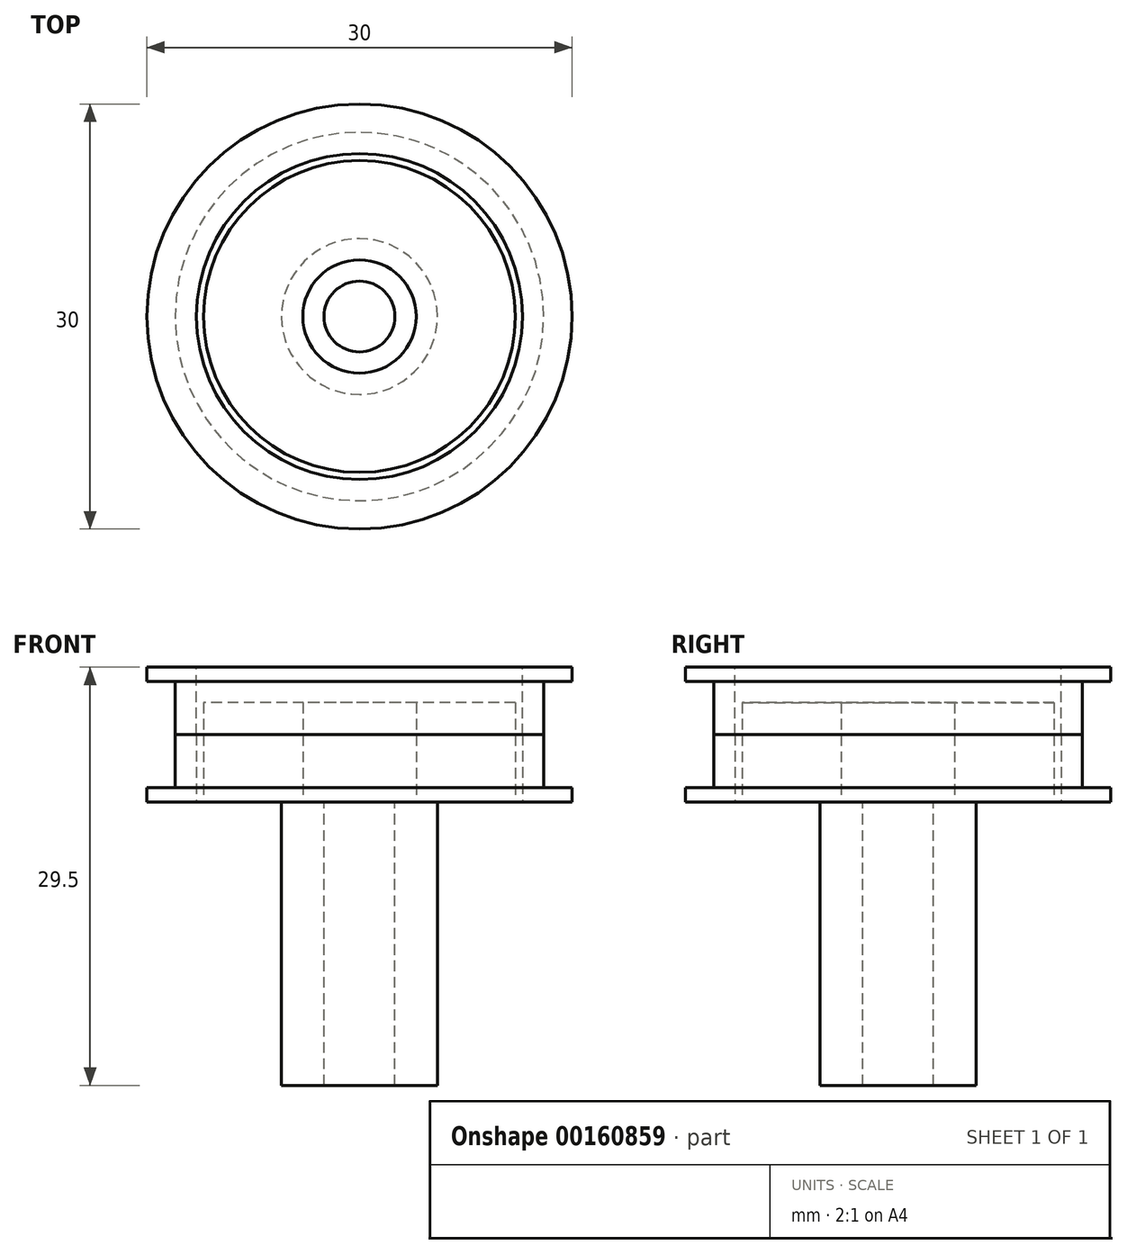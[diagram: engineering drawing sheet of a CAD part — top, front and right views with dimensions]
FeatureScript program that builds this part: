
annotation { "Feature Type Name" : "Feature", "Feature Type Description" : "" }
export const myFeature = defineFeature(function(context is Context, id is Id, definition is map)
    precondition{}
    {
        {
            var Q0;
            Q0=qCreatedBy(makeId("Top.planeOp"),FACE);
            var sketch = newSketch(context, id + "F0", { "sketchPlane" : qUnion([Q0])});
            skCircle(sketch, "E0", {"center": v(0, 0) * mm, "radius": 4 * mm});
            skCircle(sketch, "E1", {"center": v(0, 0) * mm, "radius": 11 * mm});
            skSolve(sketch);
        }
        {
            var Q0;
            Q0 = qSketchRegion(id + "F0", true);
            extrude(context, id + "F1", {"entities" : qUnion([Q0]), "depth" : 7 * mm});
        }
        {
            var Q0;
            Q0=qCreatedBy(makeId("Top.planeOp"),FACE);
            var Q1;
            Q1=qCreatedBy(makeId("Top.planeOp"),FACE);
            var sketch = newSketch(context, id + "F2", { "sketchPlane" : qUnion([Q0, Q1])});
            skCircle(sketch, "E2", {"center": v(0, 0) * mm, "radius": 2.5 * mm});
            skCircle(sketch, "E3", {"center": v(0, 0) * mm, "radius": 5.5 * mm});
            skSolve(sketch);
        }
        {
            var Q0;
            Q0 = qSketchRegion(id + "F2", true);
            extrude(context, id + "F3", {"entities" : qUnion([Q0]), "oppositeDirection" : true, "depth" : 20 * mm});
        }
        {
            var Q0;
            Q0=qCreatedBy(makeId("Top.planeOp"),FACE);
            var sketch = newSketch(context, id + "F4", { "sketchPlane" : qUnion([Q0])});
            skCircle(sketch, "E4", {"center": v(0, 0) * mm, "radius": 11.5 * mm});
            skCircle(sketch, "E5", {"center": v(0, 0) * mm, "radius": 13 * mm});
            skSolve(sketch);
        }
        {
            var Q0;
            Q0 = qSketchRegion(id + "F4", true);
            extrude(context, id + "F5", {"entities" : qUnion([Q0]), "depth" : 4.75 * mm});
        }
        {
            var Q0;
            Q0=qCreatedBy(makeId("Top.planeOp"),FACE);
            var sketch = newSketch(context, id + "F6", { "sketchPlane" : qUnion([Q0])});
            skCircle(sketch, "E6", {"center": v(0, 0) * mm, "radius": 13 * mm});
            skCircle(sketch, "E7", {"center": v(0, 0) * mm, "radius": 15 * mm});
            skSolve(sketch);
        }
        {
            var Q0;
            Q0 = qSketchRegion(id + "F6", true);
            extrude(context, id + "F7", {"entities" : qUnion([Q0]), "operationType" : NewBodyOperationType.ADD, "depth" : 1 * mm});
        }
        {
            var Q0;
            Q0=makeQuery(id+"F5.opExtrude","SWEPT_BODY",BODY,{"disambiguationData":[OSD([sQuery(id+"F4.wireOp",EDGE,"E4"),sQuery(id+"F4.wireOp",EDGE,"E5")])]});
            var Q1;
            Q1=makeQuery(id+"F5.opExtrude","CAP_FACE",FACE,{"disambiguationData":[OSD([sQuery(id+"F4.wireOp",EDGE,"E4"),sQuery(id+"F4.wireOp",EDGE,"E5")])],"isStart":false});
            mirror(context, id + "F8", {"operationType" : NewBodyOperationType.ADD, "entities" : qUnion([Q0]), "mirrorPlane" : qUnion([Q1])});
        }
    });
